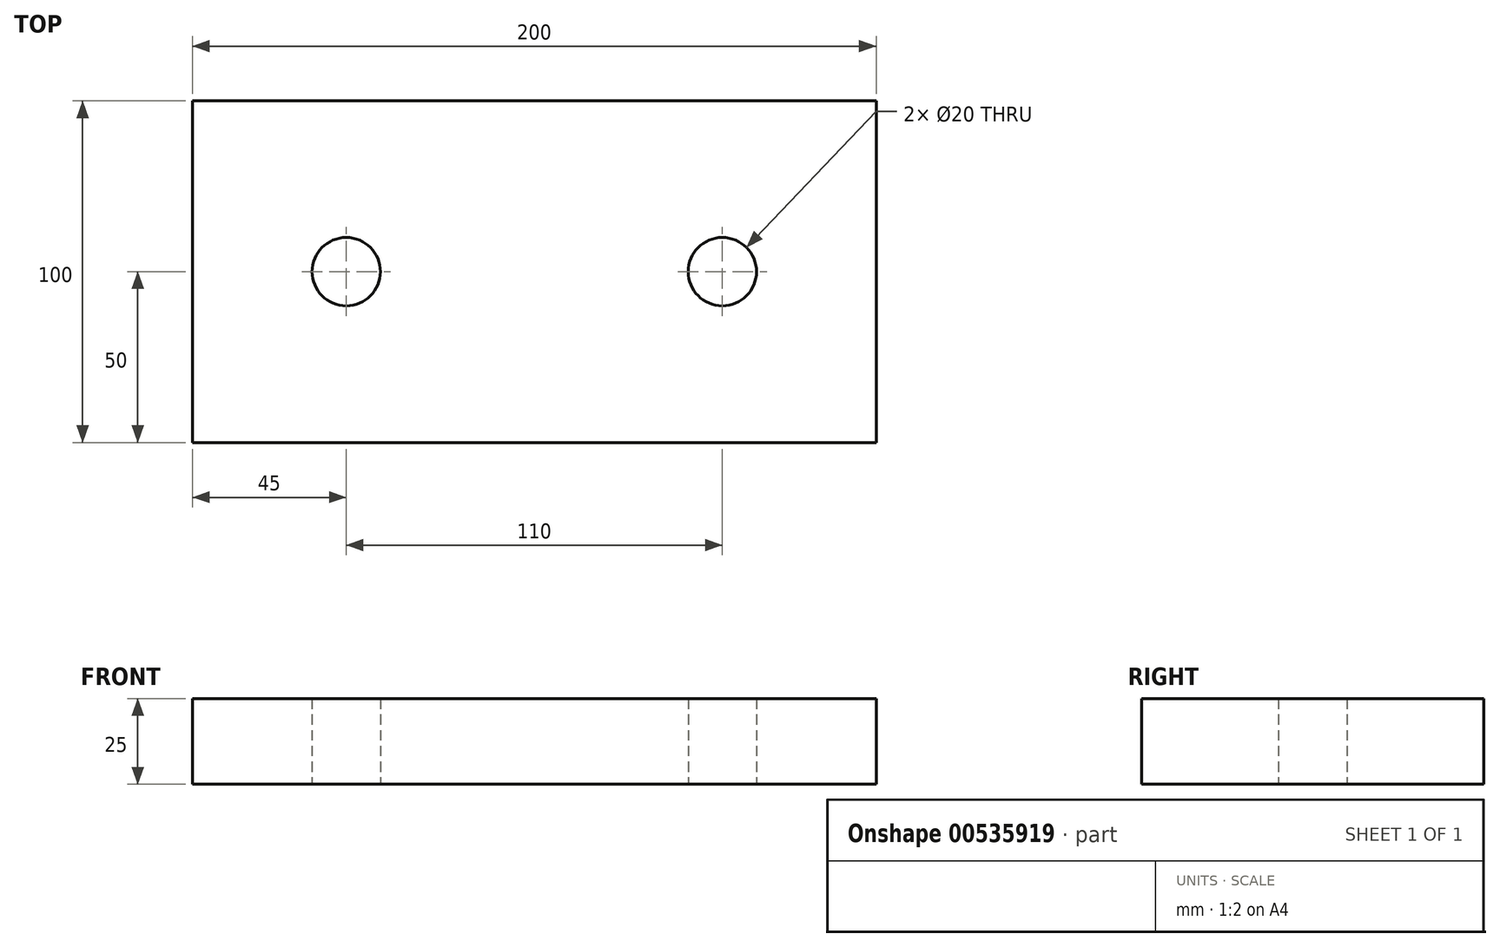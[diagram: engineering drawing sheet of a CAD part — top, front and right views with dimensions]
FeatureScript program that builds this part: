
annotation { "Feature Type Name" : "Feature", "Feature Type Description" : "" }
export const myFeature = defineFeature(function(context is Context, id is Id, definition is map)
    precondition{}
    {
        {
            var Q0;
            Q0=qCreatedBy(makeId("Top.planeOp"),FACE);
            var sketch = newSketch(context, id + "F0", { "sketchPlane" : qUnion([Q0])});
            skLineSegment(sketch, "E0.bottom", {"start": v(0, 0) * mm, "end": v(200, 0) * mm});
            skLineSegment(sketch, "E0.top", {"start": v(0, 100) * mm, "end": v(200, 100) * mm});
            skLineSegment(sketch, "E0.left", {"start": v(0, 0) * mm, "end": v(0, 100) * mm});
            skLineSegment(sketch, "E0.right", {"start": v(200, 0) * mm, "end": v(200, 100) * mm});
            skPoint(sketch, "E1", {"position": v(45, 50) * mm});
            skPoint(sketch, "E1.positionSnap0", {"position": v(0, 50) * mm});
            skPoint(sketch, "E2", {"position": v(200, 50) * mm});
            skPoint(sketch, "E3", {"position": v(155, 50) * mm});
            skCircle(sketch, "E4", {"center": v(45, 50) * mm, "radius": 10 * mm});
            skCircle(sketch, "E5", {"center": v(155, 50) * mm, "radius": 10 * mm});
            skPoint(sketch, "E6", {"position": v(100, 100) * mm});
            skPoint(sketch, "E7", {"position": v(100, 0) * mm});
            skLineSegment(sketch, "E8", {"start": v(100, 100) * mm, "end": v(100, 0) * mm});
            skPoint(sketch, "E9", {"position": v(45, 0) * mm});
            skSolve(sketch);
        }
        {
            var Q0;
            Q0 = qSketchRegion(id + "F0", true);
            extrude(context, id + "F1", {"entities" : qUnion([Q0]), "depth" : 25 * mm, "offsetDistance" : 25 * mm});
        }
    });
